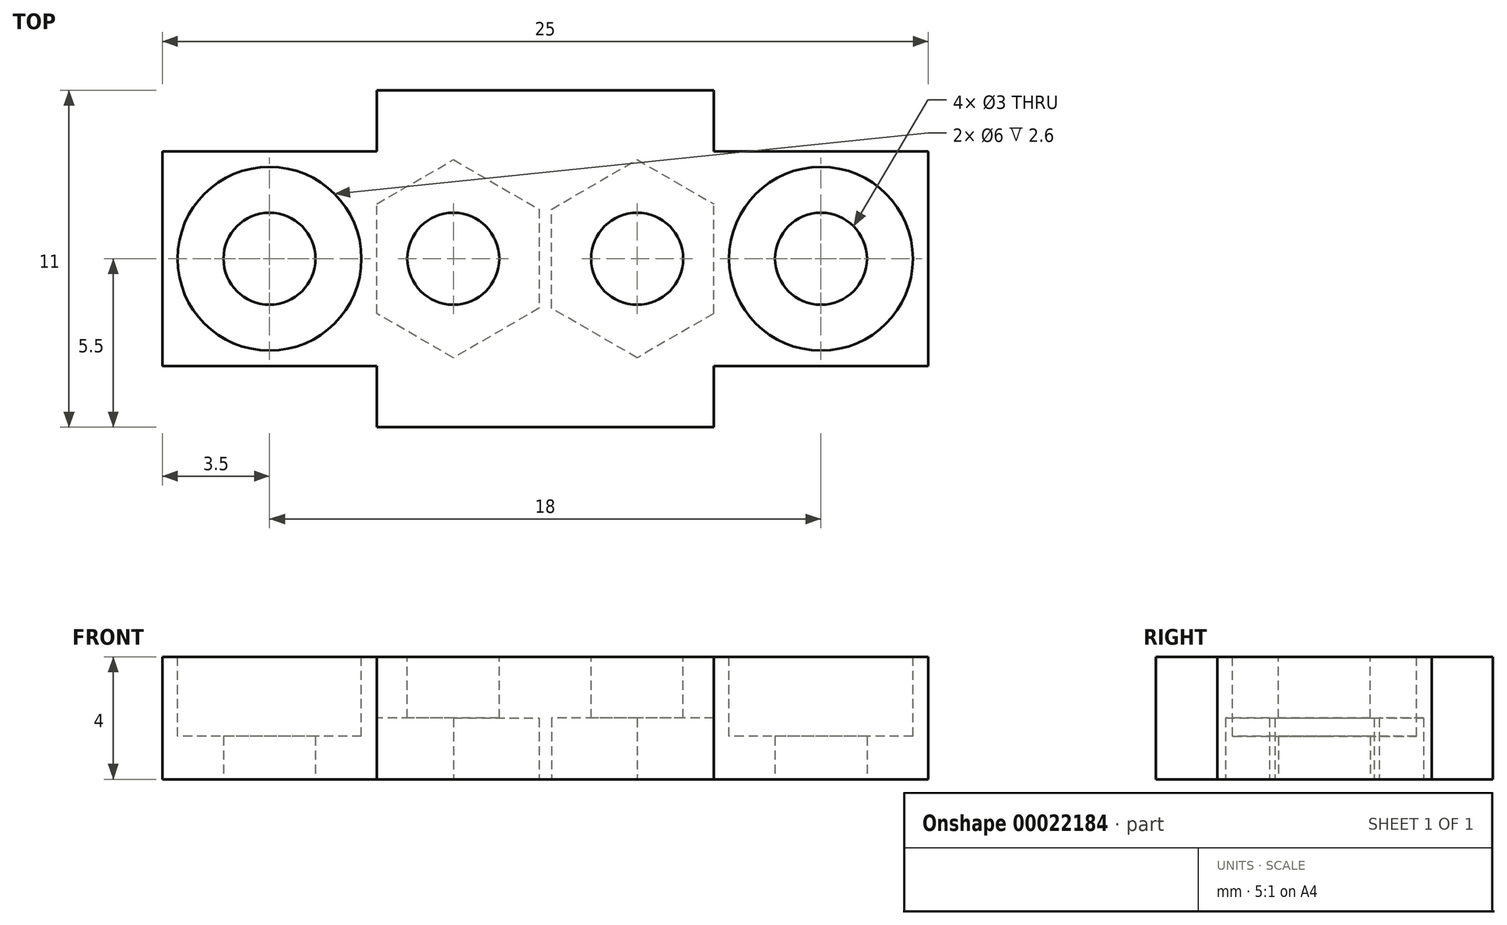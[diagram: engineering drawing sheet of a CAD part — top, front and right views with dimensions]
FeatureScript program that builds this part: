
annotation { "Feature Type Name" : "Feature", "Feature Type Description" : "" }
export const myFeature = defineFeature(function(context is Context, id is Id, definition is map)
    precondition{}
    {
        {
            var Q0;
            Q0=qCreatedBy(makeId("Top.planeOp"),FACE);
            var sketch = newSketch(context, id + "F0", { "sketchPlane" : qUnion([Q0])});
            skLineSegment(sketch, "E0.rect.bottom", {"start": v(-5.5, -5.5) * mm, "end": v(5.5, -5.5) * mm});
            skLineSegment(sketch, "E0.rect.top", {"start": v(-5.5, 5.5) * mm, "end": v(5.5, 5.5) * mm});
            skLineSegment(sketch, "E0.rect.left", {"start": v(-5.5, -5.5) * mm, "end": v(-5.5, 5.5) * mm});
            skLineSegment(sketch, "E0.rect.right", {"start": v(5.5, -5.5) * mm, "end": v(5.5, 5.5) * mm});
            skPoint(sketch, "E0.rect.middle", {"position": v(0, 0) * mm});
            skLineSegment(sketch, "E1.bottom", {"start": v(-5.5, 3.5) * mm, "end": v(-12.5, 3.5) * mm});
            skLineSegment(sketch, "E1.top", {"start": v(-5.5, -3.5) * mm, "end": v(-12.5, -3.5) * mm});
            skLineSegment(sketch, "E1.left", {"start": v(-5.5, 3.5) * mm, "end": v(-5.5, -3.5) * mm});
            skLineSegment(sketch, "E1.right", {"start": v(-12.5, 3.5) * mm, "end": v(-12.5, -3.5) * mm});
            skLineSegment(sketch, "E2", {"start": v(-9, -3.5) * mm, "end": v(-9, 3.5) * mm, "construction": true});
            skCircle(sketch, "E3", {"center": v(-9, 0) * mm, "radius": 3.05 * mm});
            skCircle(sketch, "E4", {"center": v(-9, 0) * mm, "radius": 1.5 * mm});
            skLineSegment(sketch, "E5.1.0", {"start": v(5.5, 3.5) * mm, "end": v(12.5, 3.5) * mm});
            skLineSegment(sketch, "E5.1.1", {"start": v(12.5, -3.5) * mm, "end": v(12.5, 3.5) * mm});
            skLineSegment(sketch, "E5.1.2", {"start": v(5.5, -3.5) * mm, "end": v(12.5, -3.5) * mm});
            skLineSegment(sketch, "E5.1.3", {"start": v(5.5, -3.5) * mm, "end": v(5.5, 3.5) * mm});
            skCircle(sketch, "E5.1.4", {"center": v(9, 0) * mm, "radius": 3.05 * mm});
            skCircle(sketch, "E5.1.5", {"center": v(9, 0) * mm, "radius": 1.5 * mm});
            skSolve(sketch);
        }
        {
            var Q0;
            Q0 = qSketchRegion(id + "F0", true);
            var Q1;
            Q1=makeQuery(id+"F0.imprint","IMPRINT",FACE,{"disambiguationData":[TD([[makeQuery(id+"F0.imprint","IMPRINT",EDGE,{"derivedFrom":sQuery(id+"F0.wireOp",EDGE,"E3")}),1.0]])]});
            var Q2;
            Q2=makeQuery(id+"F0.imprint","IMPRINT",FACE,{"disambiguationData":[TD([[makeQuery(id+"F0.imprint","IMPRINT",EDGE,{"derivedFrom":sQuery(id+"F0.wireOp",EDGE,"E5.1.4")}),1.0]])]});
            extrude(context, id + "F1", {"entities" : qUnion([Q0, Q1, Q2]), "depth" : 4 * mm});
        }
        {
            var Q0;
            Q0=makeQuery(id+"F1.opExtrude","CAP_FACE",FACE,{"disambiguationData":[OSD([sQuery(id+"F0.wireOp",EDGE,"E0.rect.bottom"),sQuery(id+"F0.wireOp",EDGE,"E0.rect.top"),sQuery(id+"F0.wireOp",EDGE,"E0.rect.left"),sQuery(id+"F0.wireOp",EDGE,"E0.rect.right"),sQuery(id+"F0.wireOp",EDGE,"E1.bottom"),sQuery(id+"F0.wireOp",EDGE,"E1.top"),sQuery(id+"F0.wireOp",EDGE,"E1.right"),sQuery(id+"F0.wireOp",EDGE,"E4"),sQuery(id+"F0.wireOp",EDGE,"E5.1.0"),sQuery(id+"F0.wireOp",EDGE,"E5.1.1"),sQuery(id+"F0.wireOp",EDGE,"E5.1.2"),sQuery(id+"F0.wireOp",EDGE,"E5.1.5")])],"isStart":false});
            var sketch = newSketch(context, id + "F2", { "sketchPlane" : qUnion([Q0])});
            skCircle(sketch, "E6", {"center": v(-9, 0) * mm, "radius": 3 * mm});
            skCircle(sketch, "E7", {"center": v(9, 0) * mm, "radius": 3 * mm});
            skSolve(sketch);
        }
        {
            var Q0;
            Q0 = qSketchRegion(id + "F2", true);
            extrude(context, id + "F3", {"entities" : qUnion([Q0]), "operationType" : NewBodyOperationType.REMOVE, "oppositeDirection" : true, "depth" : 2.6 * mm});
        }
        {
            var Q0;
            Q0=makeQuery(id+"F1.opExtrude","CAP_FACE",FACE,{"disambiguationData":[OSD([sQuery(id+"F0.wireOp",EDGE,"E0.rect.bottom"),sQuery(id+"F0.wireOp",EDGE,"E0.rect.top"),sQuery(id+"F0.wireOp",EDGE,"E0.rect.left"),sQuery(id+"F0.wireOp",EDGE,"E0.rect.right"),sQuery(id+"F0.wireOp",EDGE,"E1.bottom"),sQuery(id+"F0.wireOp",EDGE,"E1.top"),sQuery(id+"F0.wireOp",EDGE,"E1.right"),sQuery(id+"F0.wireOp",EDGE,"E4"),sQuery(id+"F0.wireOp",EDGE,"E5.1.0"),sQuery(id+"F0.wireOp",EDGE,"E5.1.1"),sQuery(id+"F0.wireOp",EDGE,"E5.1.2"),sQuery(id+"F0.wireOp",EDGE,"E5.1.5")])],"isStart":false});
            var sketch = newSketch(context, id + "F4", { "sketchPlane" : qUnion([Q0])});
            skCircle(sketch, "E8", {"center": v(3, 0) * mm, "radius": 1.5 * mm});
            skCircle(sketch, "E9", {"center": v(-3, 0) * mm, "radius": 1.5 * mm});
            skSolve(sketch);
        }
        {
            var Q0;
            Q0 = qSketchRegion(id + "F4", true);
            extrude(context, id + "F5", {"entities" : qUnion([Q0]), "operationType" : NewBodyOperationType.REMOVE, "oppositeDirection" : true, "depth" : 25 * mm});
        }
        {
            var Q0;
            {var subQ4=sQuery(id+"F0.wireOp",EDGE,"E0.rect.bottom");Q0=makeQuery(id+"F0.imprint","IMPRINT",FACE,{"disambiguationData":[TD([[makeQuery(id+"F0.imprint","IMPRINT",EDGE,{"derivedFrom":subQ4}),1.0]])]});}
            var sketch = newSketch(context, id + "F6", { "sketchPlane" : qUnion([Q0])});
            skCircle(sketch, "E10.cCircle", {"center": v(-3, 0) * mm, "radius": 2.8 * mm, "construction": true});
            skLineSegment(sketch, "E10.0", {"start": v(-0.2, -1.62) * mm, "end": v(-3, -3.23) * mm});
            skLineSegment(sketch, "E10.1", {"start": v(-3, -3.23) * mm, "end": v(-5.8, -1.62) * mm});
            skLineSegment(sketch, "E10.2", {"start": v(-5.8, -1.62) * mm, "end": v(-5.8, 1.62) * mm});
            skLineSegment(sketch, "E10.3", {"start": v(-5.8, 1.62) * mm, "end": v(-3, 3.23) * mm});
            skLineSegment(sketch, "E10.4", {"start": v(-3, 3.23) * mm, "end": v(-0.2, 1.62) * mm});
            skLineSegment(sketch, "E10.5", {"start": v(-0.2, 1.62) * mm, "end": v(-0.2, -1.62) * mm});
            skPoint(sketch, "E10.0.midPoint", {"position": v(-1.6, -2.42) * mm});
            skCircle(sketch, "E11.cCircle", {"center": v(3, 0) * mm, "radius": 2.8 * mm, "construction": true});
            skLineSegment(sketch, "E11.0", {"start": v(5.8, -1.62) * mm, "end": v(3, -3.23) * mm});
            skLineSegment(sketch, "E11.1", {"start": v(3, -3.23) * mm, "end": v(0.2, -1.62) * mm});
            skLineSegment(sketch, "E11.2", {"start": v(0.2, -1.62) * mm, "end": v(0.2, 1.62) * mm});
            skLineSegment(sketch, "E11.3", {"start": v(0.2, 1.62) * mm, "end": v(3, 3.23) * mm});
            skLineSegment(sketch, "E11.4", {"start": v(3, 3.23) * mm, "end": v(5.8, 1.62) * mm});
            skLineSegment(sketch, "E11.5", {"start": v(5.8, 1.62) * mm, "end": v(5.8, -1.62) * mm});
            skPoint(sketch, "E11.0.midPoint", {"position": v(4.4, -2.42) * mm});
            skSolve(sketch);
        }
        {
            var Q0;
            {var subQ6=sQuery(id+"F6.wireOp",EDGE,"E11.1");Q0=makeQuery(id+"F6.imprint","IMPRINT",FACE,{"disambiguationData":[TD([[makeQuery(id+"F6.imprint","IMPRINT",EDGE,{"derivedFrom":subQ6}),-1.0]])]});}
            var Q1;
            {var subQ6=sQuery(id+"F6.wireOp",EDGE,"E10.0");Q1=makeQuery(id+"F6.imprint","IMPRINT",FACE,{"disambiguationData":[TD([[makeQuery(id+"F6.imprint","IMPRINT",EDGE,{"derivedFrom":subQ6}),-1.0]])]});}
            extrude(context, id + "F7", {"entities" : qUnion([Q0, Q1]), "operationType" : NewBodyOperationType.REMOVE, "depth" : 2 * mm});
        }
    });
